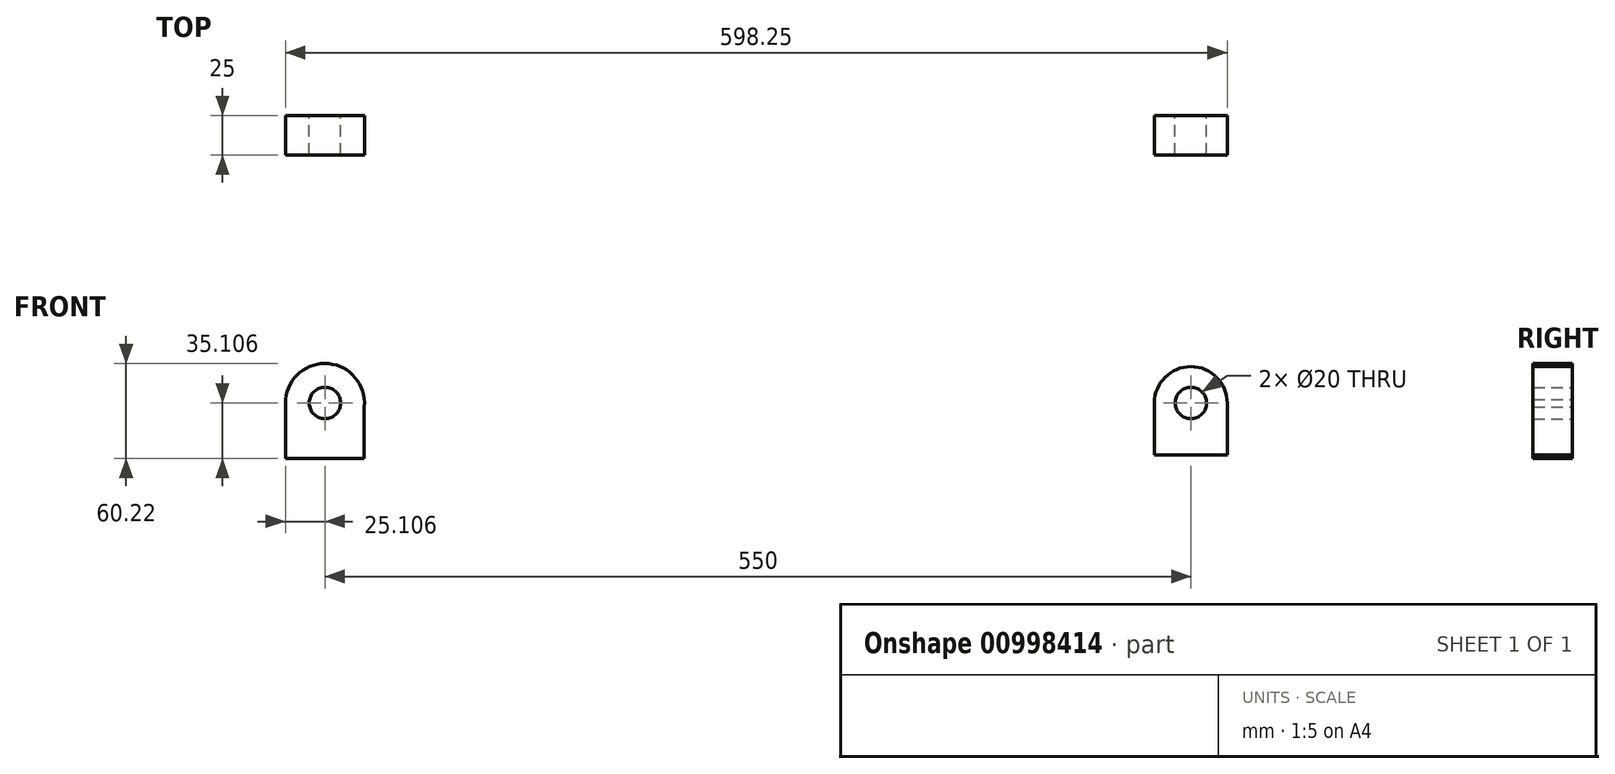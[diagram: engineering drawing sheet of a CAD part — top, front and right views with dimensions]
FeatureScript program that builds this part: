
annotation { "Feature Type Name" : "Feature", "Feature Type Description" : "" }
export const myFeature = defineFeature(function(context is Context, id is Id, definition is map)
    precondition{}
    {
        {
            var Q0;
            Q0=qCreatedBy(makeId("Front.planeOp"),FACE);
            var sketch = newSketch(context, id + "F0", { "sketchPlane" : qUnion([Q0])});
            skCircle(sketch, "E0", {"center": v(98.63, 310.96) * mm, "radius": 10 * mm});
            skCircle(sketch, "E1", {"center": v(648.63, 310.96) * mm, "radius": 10 * mm});
            skLineSegment(sketch, "E2.bottom", {"start": v(73.52, 313.3) * mm, "end": v(123.63, 313.3) * mm});
            skLineSegment(sketch, "E2.top", {"start": v(73.52, 275.85) * mm, "end": v(123.63, 275.85) * mm});
            skLineSegment(sketch, "E2.left", {"start": v(73.52, 313.3) * mm, "end": v(73.52, 275.85) * mm});
            skLineSegment(sketch, "E2.right", {"start": v(123.63, 313.3) * mm, "end": v(123.63, 275.85) * mm});
            skCircle(sketch, "E3", {"center": v(98.63, 310.96) * mm, "radius": 25.11 * mm});
            skCircle(sketch, "E4", {"center": v(648.63, 310.96) * mm, "radius": 23.14 * mm});
            skLineSegment(sketch, "E5.bottom", {"start": v(625.48, 310.96) * mm, "end": v(671.77, 310.96) * mm});
            skLineSegment(sketch, "E5.top", {"start": v(625.48, 277.81) * mm, "end": v(671.77, 277.81) * mm});
            skLineSegment(sketch, "E5.left", {"start": v(625.48, 310.96) * mm, "end": v(625.48, 277.81) * mm});
            skLineSegment(sketch, "E5.right", {"start": v(671.77, 310.96) * mm, "end": v(671.77, 277.81) * mm});
            skSolve(sketch);
        }
        {
            var Q0;
            Q0 = qSketchRegion(id + "F0", true);
            extrude(context, id + "F1", {"entities" : qUnion([Q0]), "depth" : 25 * mm, "offsetDistance" : 25 * mm});
        }
    });
